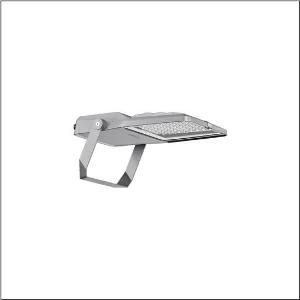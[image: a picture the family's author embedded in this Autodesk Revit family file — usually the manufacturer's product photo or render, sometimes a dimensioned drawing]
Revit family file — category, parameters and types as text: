
# Revit family: floodlight_fl_21_mini___pl64_5xa7776c2e1a_42f0
name_source: partatom
category: Lighting Fixtures
units: mm (PartAtom-declared; Revit-internal decimal feet)

## family parameters
Cut with Voids When Loaded = No
Host = Face
Light Source = No
Part Type = Normal
Room Calculation Point = No
Round Connector Dimension = Use Diameter
Shared = No

## types (1)
- --- (1 x LED, 11770 lm, 89 W, 3000K)
    Apparent Load = 89 VA
    CIE Flux Codes = 28 80 98 100 100
    Color Rendering = 70
    Color Temperature = 3000K
    Default Elevation = 1800 mm
    Description = Floodlight FL 21 mini, floodlight, primary light control with lens, of PMMA, primary optical cover: protective disc, of toughened safety glass, transparent, light distribution: PL64, light emission: direct distribution, installation type: surface-mounted, LED, High Power LED, rated luminous flux: 11.770lm, luminous efficacy: 132lm/W, light colour: 730, colour temperature: 3000K, control: flexible luminous flux parameterisation, time-dependent luminous flux control, constant luminous flux control, overheat protection, presetting dimming logarithmic, with terminal, 6-pole, mains connection: 220..240V, AC, 50/60Hz, start of lifetime: 89W, end of service life: 94W, reduction: 43W, luminaire housing, of diecast aluminium, powder-coated, Siteco® metallic grey (DB 702S), corrosivity category C5 mid according to DIN EN ISO 12944, sealing non-destructively replaceable, mounting bracket, of steel, galvanised, powder-coated, Siteco® metallic grey (DB 702S), Smart Interface below and above, protection rating (complete): IP66, insulation class (complete): insulation class II (safety insulation), certification: CE, ENEC, VDE, protection symbol: D, impact resistance: IK08, permissible operating ambient temperature: -40..+40°C, permissible operating ambient temperature for outdoor applications: -40..+50°C, standard: DIN EN 12944, LABS conformity tested according to VDMA 24364:2018-05, packaging unit: 1 piece

Light Distribution: PL64
    Height = 70 mm
    Lamp = 1 x LED
    Lamp Light Flux = 11770 lm
    Lamp Power = 89 W
    Lamp count = 1
    Length = 485 mm
    Luminous efficacy = 132 lm/W
    Manufacturer = Siteco
    ModVariant = No
    Model = 5XA7776C2E1A
    Number of Poles = 1
    OnlyDefault = Yes
    Power Factor = 1
    Product Name = Floodlight FL 21 mini | PL64
    Product group = floodlight | pylon annexe
    ProductGroupID = 6200
    Protection Class = Protection class II
    Protection Degree = IP 66
    RLX_Detail_Level = 1
    RLX_Emergency_Light_Flux = 0 lm
    RLX_Emergency_Type = 0
    RLX_Emergency_Type_DB = No
    RlxData = <blob elided: 95929 chars, md5=dbb77b9e>
    Socket = socket
    Standby Power = 0 W
    System Light Flux = 11770 lm
    System Power = 89 W
    Type Comments = factory setting: luminous flux: 100 % | dim-lin: 254 | 456 mA
    Type Image = l_1006845.jpg
    URL = http://relux.com
    VarID = @adj_097679
    Voltage = 0 V
    Weight = 0.00 kg
    Width = 337 mm

## geometry (parser evidence)
native form markers: Blend x4, Sweep x13
no freeform markers — native parametric forms only
